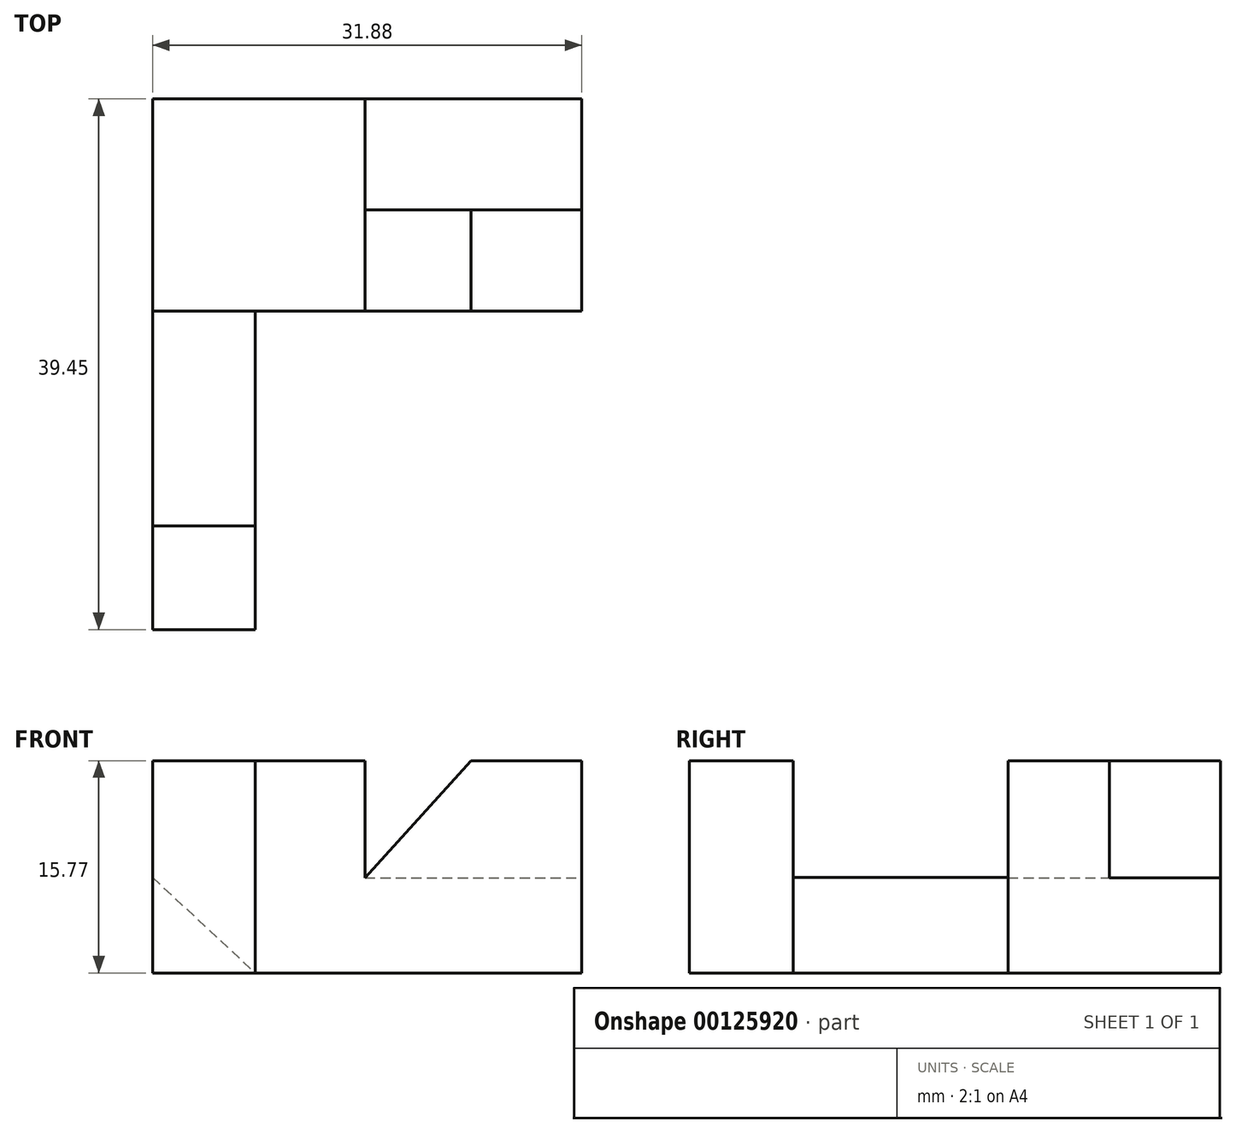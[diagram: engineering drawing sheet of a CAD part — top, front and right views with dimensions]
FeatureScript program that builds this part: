
annotation { "Feature Type Name" : "Feature", "Feature Type Description" : "" }
export const myFeature = defineFeature(function(context is Context, id is Id, definition is map)
    precondition{}
    {
        {
            var Q0;
            Q0=qCreatedBy(makeId("Front.planeOp"),FACE);
            var sketch = newSketch(context, id + "F0", { "sketchPlane" : qUnion([Q0])});
            skLineSegment(sketch, "E0.bottom", {"start": v(0, 0) * mm, "end": v(15.77, 0) * mm});
            skLineSegment(sketch, "E0.top", {"start": v(0, 15.77) * mm, "end": v(15.77, 15.77) * mm});
            skLineSegment(sketch, "E0.left", {"start": v(0, 0) * mm, "end": v(0, 15.77) * mm});
            skLineSegment(sketch, "E0.right", {"start": v(15.77, 0) * mm, "end": v(15.77, 15.77) * mm});
            skSolve(sketch);
        }
        {
            var Q0;
            Q0=qSketchRegion(id+"F0",true);
            extrude(context, id + "F1", {"entities" : qUnion([Q0]), "depth" : 15.77 * mm});
        }
        {
            var Q0;
            Q0=makeQuery(id+"F1.opExtrude","CAP_FACE",FACE,{"disambiguationData":[OSD([sQuery(id+"F0.wireOp",EDGE,"E0.bottom"),sQuery(id+"F0.wireOp",EDGE,"E0.top"),sQuery(id+"F0.wireOp",EDGE,"E0.left"),sQuery(id+"F0.wireOp",EDGE,"E0.right")])],"isStart":false});
            var sketch = newSketch(context, id + "F2", { "sketchPlane" : qUnion([Q0])});
            skLineSegment(sketch, "E1", {"start": v(0, 0) * mm, "end": v(7.62, 0) * mm});
            skLineSegment(sketch, "E2", {"start": v(0, 0) * mm, "end": v(0, 7.09) * mm});
            skLineSegment(sketch, "E3", {"start": v(0, 7.09) * mm, "end": v(7.62, 0) * mm});
            skSolve(sketch);
        }
        {
            var Q0;
            Q0=qSketchRegion(id+"F2",true);
            extrude(context, id + "F3", {"entities" : qUnion([Q0]), "operationType" : NewBodyOperationType.ADD, "depth" : 15.95 * mm});
        }
        {
            var Q0;
            Q0=makeQuery(id+"F3.opExtrude","CAP_FACE",FACE,{"disambiguationData":[OSD([sQuery(id+"F2.wireOp",EDGE,"E1"),sQuery(id+"F2.wireOp",EDGE,"E2"),sQuery(id+"F2.wireOp",EDGE,"E3")])],"isStart":false});
            var sketch = newSketch(context, id + "F4", { "sketchPlane" : qUnion([Q0])});
            skLineSegment(sketch, "E4.bottom", {"start": v(0, 0) * mm, "end": v(7.62, 0) * mm});
            skLineSegment(sketch, "E4.top", {"start": v(0, 15.77) * mm, "end": v(7.62, 15.77) * mm});
            skLineSegment(sketch, "E4.left", {"start": v(0, 0) * mm, "end": v(0, 15.77) * mm});
            skLineSegment(sketch, "E4.right", {"start": v(7.62, 0) * mm, "end": v(7.62, 15.77) * mm});
            skSolve(sketch);
        }
        {
            var Q0;
            {var subQ0=sQuery(id+"F4.wireOp",EDGE,"E4.top");Q0=makeQuery(id+"F4.imprint","IMPRINT",FACE,{"disambiguationData":[TD([[makeQuery(id+"F4.imprint","IMPRINT",EDGE,{"derivedFrom":subQ0}),-1.0]])]});}
            var Q1;
            {var subQ0=sQuery(id+"F4.wireOp",EDGE,"E4.bottom");Q1=makeQuery(id+"F4.imprint","IMPRINT",FACE,{"disambiguationData":[TD([[makeQuery(id+"F4.imprint","IMPRINT",EDGE,{"derivedFrom":subQ0}),1.0]])]});}
            extrude(context, id + "F5", {"entities" : qUnion([Q0, Q1]), "operationType" : NewBodyOperationType.ADD, "depth" : 7.72 * mm});
        }
        {
            var Q0;
            Q0=makeQuery(id+"F1.opExtrude","SWEPT_FACE",FACE,{"disambiguationData":[OSD([sQuery(id+"F0.wireOp",EDGE,"E0.right")])]});
            var sketch = newSketch(context, id + "F6", { "sketchPlane" : qUnion([Q0])});
            skLineSegment(sketch, "E5.bottom", {"start": v(-15.77, 0) * mm, "end": v(0, 0) * mm});
            skLineSegment(sketch, "E5.top", {"start": v(-15.77, 7.05) * mm, "end": v(0, 7.05) * mm});
            skLineSegment(sketch, "E5.left", {"start": v(-15.77, 0) * mm, "end": v(-15.77, 7.05) * mm});
            skLineSegment(sketch, "E5.right", {"start": v(0, 0) * mm, "end": v(0, 7.05) * mm});
            skSolve(sketch);
        }
        {
            var Q0;
            Q0=makeQuery(id+"F6.imprint","IMPRINT",FACE,{"disambiguationData":[TD([[makeQuery(id+"F6.imprint","IMPRINT",EDGE,{"derivedFrom":sQuery(id+"F6.wireOp",EDGE,"E5.bottom")}),1.0]])]});
            extrude(context, id + "F7", {"entities" : qUnion([Q0]), "operationType" : NewBodyOperationType.ADD, "depth" : 16.1 * mm});
        }
        {
            var Q0;
            Q0=makeQuery(id+"F7.opExtrude","CAP_FACE",FACE,{"disambiguationData":[OSD([sQuery(id+"F6.wireOp",EDGE,"E5.bottom"),sQuery(id+"F6.wireOp",EDGE,"E5.top"),sQuery(id+"F6.wireOp",EDGE,"E5.left"),sQuery(id+"F6.wireOp",EDGE,"E5.right")])],"isStart":false});
            var sketch = newSketch(context, id + "F8", { "sketchPlane" : qUnion([Q0])});
            skLineSegment(sketch, "E6.bottom", {"start": v(-15.77, 7.05) * mm, "end": v(-8.26, 7.05) * mm});
            skLineSegment(sketch, "E7.0", {"start": v(-15.77, 15.77) * mm, "end": v(0, 15.77) * mm});
            skLineSegment(sketch, "E8", {"start": v(-15.77, 7.05) * mm, "end": v(-15.77, 15.77) * mm});
            skLineSegment(sketch, "E9", {"start": v(-8.26, 7.05) * mm, "end": v(-8.26, 15.77) * mm});
            skLineSegment(sketch, "E10", {"start": v(-8.26, 15.77) * mm, "end": v(-15.77, 15.77) * mm});
            skSolve(sketch);
        }
        {
            var Q0;
            Q0=makeQuery(id+"F8.imprint","IMPRINT",FACE,{"disambiguationData":[TD([[makeQuery(id+"F8.imprint","IMPRINT",EDGE,{"derivedFrom":sQuery(id+"F8.wireOp",EDGE,"E6.bottom")}),1.0]])]});
            var Q1;
            Q1=makeQuery(id+"F1.opExtrude","SWEPT_FACE",FACE,{"disambiguationData":[OSD([sQuery(id+"F0.wireOp",EDGE,"E0.right")])]});
            extrude(context, id + "F9", {"entities" : qUnion([Q0]), "operationType" : NewBodyOperationType.ADD, "endBound" : BoundingType.UP_TO_SURFACE, "oppositeDirection" : true, "endBoundEntityFace" : qUnion([Q1]), "depth" : 25.4 * mm});
        }
        {
            var Q0;
            Q0=makeQuery(id+"F9.opExtrude","SWEPT_FACE",FACE,{"disambiguationData":[OSD([sQuery(id+"F8.wireOp",EDGE,"E9")])]});
            var sketch = newSketch(context, id + "F10", { "sketchPlane" : qUnion([Q0])});
            skLineSegment(sketch, "E11.0", {"start": v(-15.77, 7.05) * mm, "end": v(-15.77, 15.77) * mm});
            skLineSegment(sketch, "E12.0", {"start": v(-15.77, 15.77) * mm, "end": v(-31.88, 15.77) * mm});
            skLineSegment(sketch, "E13", {"start": v(-23.65, 15.77) * mm, "end": v(-15.77, 15.77) * mm});
            skLineSegment(sketch, "E14", {"start": v(-15.77, 7.05) * mm, "end": v(-23.65, 15.77) * mm});
            skSolve(sketch);
        }
        {
            var Q0;
            Q0=makeQuery(id+"F10.imprint","IMPRINT",FACE,{"disambiguationData":[TD([[makeQuery(id+"F10.imprint","IMPRINT",EDGE,{"derivedFrom":sQuery(id+"F10.wireOp",EDGE,"E11.0")}),1.0]])]});
            extrude(context, id + "F11", {"entities" : qUnion([Q0]), "operationType" : NewBodyOperationType.REMOVE, "oppositeDirection" : true, "depth" : 25.4 * mm});
        }
    });
